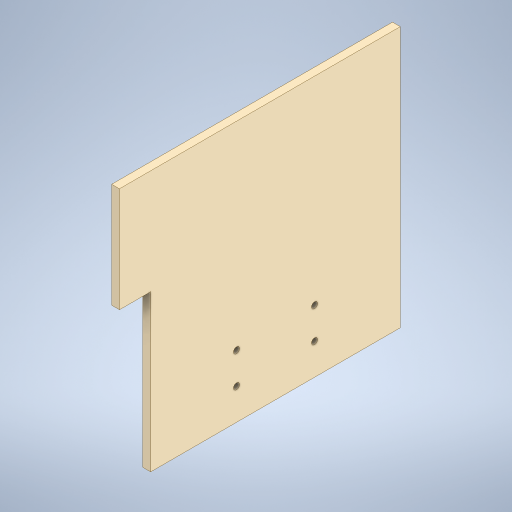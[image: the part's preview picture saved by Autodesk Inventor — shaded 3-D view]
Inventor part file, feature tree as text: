
AUTODESK INVENTOR PART (.ipt)
format: ipt  version: 2024 (Build 280153000, 153)  size: 242,176 bytes
history: native  units: mm
features: extrude x3, projected_geometry x1, sketch x1
ambient origin geometry x8: Origin, YZ Plane, XZ Plane, XY Plane, X Axis, Y Axis, Z Axis, Center Point
bodies: Solid1 (feature_tree)
feature tree (5):
  extrude  "Extrusion1"  Depth=424.5mm
  extrude  "Extrusion2"  Depth=12.7mm TaperAngle=0.0deg
  extrude  "Extrusion3"  Depth=50.8mm
  projected_geometry  "Projected Loop1"
  sketch  "Sketch3"  dims[d0=406.4mm d1=424.5mm d2=12.7mm d3=0.0mm d4=20.0mm d6=127.0mm d7=20.0mm d9=50.8mm d12=10.0mm d14=63.5mm d15=50.8mm d16=12.7mm d17=0.0mm d18=50.8mm d19=0.0mm d20=170.5mm]
